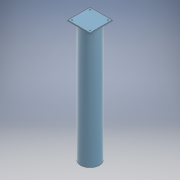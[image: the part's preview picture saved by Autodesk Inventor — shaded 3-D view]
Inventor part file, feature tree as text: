
AUTODESK INVENTOR PART (.ipt)
format: ipt  version: 2022 (Build 260153000, 153)  size: 139,776 bytes
history: native  units: mm
features: sketch x4, extrude x3, other x1, hole x1, fillet x1
ambient origin geometry x8: Origin, YZ Plane, XZ Plane, XY Plane, X Axis, Y Axis, Z Axis, Center Point
bodies: Solid1 (feature_tree)
feature tree (10):
  extrude  "InBase"  Depth=620.0mm TaperAngle=0.0deg
  extrude  "AboveBase"  Depth=8.0mm TaperAngle=0.0deg
  other  "PlateWorkPlane"
  extrude  "ConnectorPlate"  Depth=1.0mm
  hole  "BoltHoles"  [1 undecoded]
  fillet  "Fillet1"  [1 undecoded]
  sketch  "Sketch1"  dims[d0=400.0mm d1=0.0mm d2=620.0mm d3=0.0mm]
  sketch  "Sketch2"  dims[d4=0.0mm d5=8.0mm d6=0.0mm]
  sketch  "Sketch3"  dims[d7=8.0mm d8=6.0mm d9=4.0mm d10=2.0mm d11=90.0deg d12=8.0mm d13=0.0mm d14=1.0mm]
  sketch  "Sketch4"
note: 2 required parameter values undecoded (feature->parameter linkage not recoverable at this tier; creation-order binding heuristic only, values carry confidence <= 0.55)
